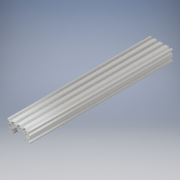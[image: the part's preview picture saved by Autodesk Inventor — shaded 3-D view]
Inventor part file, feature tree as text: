
AUTODESK INVENTOR PART (.ipt)
format: ipt  version: 2019 (Build 230136000, 136)  size: 410,624 bytes
history: native  units: mm
features: extrude x1, sketch x1
ambient origin geometry x8: Origin, YZ Plane, XZ Plane, XY Plane, X Axis, Y Axis, Z Axis, Center Point
bodies: Body1 (feature_tree)
feature tree (2):
  extrude  "Extrusion2"  [1 undecoded]
  sketch  "Sketch1"  dims[d2=500.0mm d3=0.0mm]
note: 1 required parameter value undecoded (feature->parameter linkage not recoverable at this tier; creation-order binding heuristic only, values carry confidence <= 0.55)
